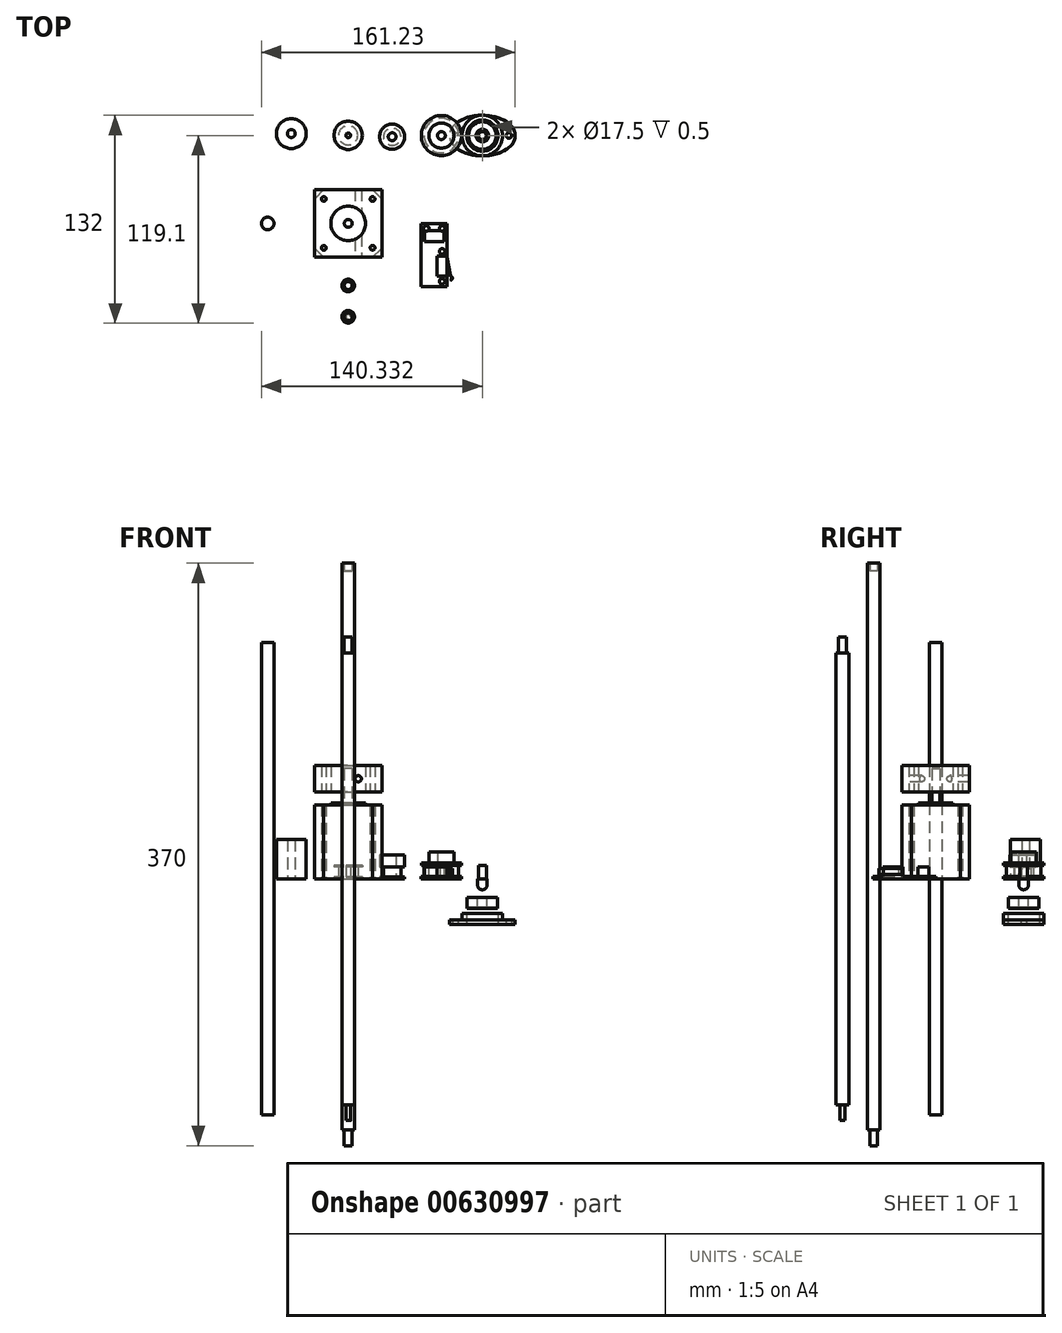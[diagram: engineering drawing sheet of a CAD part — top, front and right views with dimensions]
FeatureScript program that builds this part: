
annotation { "Feature Type Name" : "Feature", "Feature Type Description" : "" }
export const myFeature = defineFeature(function(context is Context, id is Id, definition is map)
    precondition{}
    {
        {
            var Q0;
            Q0=qCreatedBy(makeId("Top.planeOp"),FACE);
            var sketch = newSketch(context, id + "F0", { "sketchPlane" : qUnion([Q0])});
            skLineSegment(sketch, "E0.bottom", {"start": v(-21.5, 21.5) * mm, "end": v(21.5, 21.5) * mm});
            skLineSegment(sketch, "E0.top", {"start": v(-21.5, -21.5) * mm, "end": v(21.5, -21.5) * mm});
            skLineSegment(sketch, "E0.left", {"start": v(-21.5, 21.5) * mm, "end": v(-21.5, -21.5) * mm});
            skLineSegment(sketch, "E0.right", {"start": v(21.5, 21.5) * mm, "end": v(21.5, -21.5) * mm});
            skPoint(sketch, "E0.middle", {"position": v(0, 0) * mm});
            skLineSegment(sketch, "E1.bottom", {"start": v(15.5, 15.5) * mm, "end": v(-15.5, 15.5) * mm, "construction": true});
            skLineSegment(sketch, "E1.top", {"start": v(15.5, -15.5) * mm, "end": v(-15.5, -15.5) * mm, "construction": true});
            skLineSegment(sketch, "E1.left", {"start": v(15.5, 15.5) * mm, "end": v(15.5, -15.5) * mm, "construction": true});
            skLineSegment(sketch, "E1.right", {"start": v(-15.5, 15.5) * mm, "end": v(-15.5, -15.5) * mm, "construction": true});
            skCircle(sketch, "E2", {"center": v(-15.5, 15.5) * mm, "radius": 1.5 * mm});
            skCircle(sketch, "E3", {"center": v(15.5, 15.5) * mm, "radius": 1.5 * mm});
            skCircle(sketch, "E4", {"center": v(15.5, -15.5) * mm, "radius": 1.5 * mm});
            skCircle(sketch, "E5", {"center": v(-15.5, -15.5) * mm, "radius": 1.5 * mm});
            skSolve(sketch);
        }
        {
            var Q0;
            Q0=makeQuery(id+"F0.imprint","IMPRINT",FACE,{"disambiguationData":[TD([[makeQuery(id+"F0.imprint","IMPRINT",EDGE,{"derivedFrom":sQuery(id+"F0.wireOp",EDGE,"E0.bottom")}),-1.0]])]});
            extrude(context, id + "F1", {"entities" : qUnion([Q0]), "depth" : 47 * mm, "offsetDistance" : 25 * mm});
        }
        {
            var Q0;
            Q0=makeQuery(id+"F1.opExtrude","CAP_FACE",FACE,{"disambiguationData":[OSD([sQuery(id+"F0.wireOp",EDGE,"E0.bottom"),sQuery(id+"F0.wireOp",EDGE,"E0.top"),sQuery(id+"F0.wireOp",EDGE,"E0.left"),sQuery(id+"F0.wireOp",EDGE,"E0.right")])],"isStart":false});
            var sketch = newSketch(context, id + "F2", { "sketchPlane" : qUnion([Q0])});
            skCircle(sketch, "E6", {"center": v(0, 0) * mm, "radius": 11 * mm});
            skCircle(sketch, "E7", {"center": v(0, 0) * mm, "radius": 2.5 * mm});
            skSolve(sketch);
        }
        {
            var Q0;
            Q0=makeQuery(id+"F2.imprint","IMPRINT",FACE,{"disambiguationData":[TD([[makeQuery(id+"F2.imprint","IMPRINT",EDGE,{"derivedFrom":sQuery(id+"F2.wireOp",EDGE,"E7")}),1.0]])]});
            extrude(context, id + "F3", {"entities" : qUnion([Q0]), "operationType" : NewBodyOperationType.ADD, "depth" : 23 * mm, "offsetDistance" : 25 * mm});
        }
        {
            var Q0;
            Q0=makeQuery(id+"F2.imprint","IMPRINT",FACE,{"disambiguationData":[TD([[makeQuery(id+"F2.imprint","IMPRINT",EDGE,{"derivedFrom":sQuery(id+"F2.wireOp",EDGE,"E6")}),1.0]])]});
            extrude(context, id + "F4", {"entities" : qUnion([Q0]), "operationType" : NewBodyOperationType.ADD, "depth" : 1 * mm, "offsetDistance" : 25 * mm});
        }
        {
            var Q0;
            Q0=makeQuery(id+"F1.opExtrude","SWEPT_EDGE",EDGE,{"disambiguationData":[OSD([sQuery(id+"F0.wireOp",EDGE,"E0.top"),sQuery(id+"F0.wireOp",EDGE,"E0.right")])]});
            var Q1;
            Q1=makeQuery(id+"F1.opExtrude","SWEPT_EDGE",EDGE,{"disambiguationData":[OSD([sQuery(id+"F0.wireOp",EDGE,"E0.top"),sQuery(id+"F0.wireOp",EDGE,"E0.left")])]});
            var Q2;
            Q2=makeQuery(id+"F1.opExtrude","SWEPT_EDGE",EDGE,{"disambiguationData":[OSD([sQuery(id+"F0.wireOp",EDGE,"E0.bottom"),sQuery(id+"F0.wireOp",EDGE,"E0.left")])]});
            var Q3;
            Q3=makeQuery(id+"F1.opExtrude","SWEPT_EDGE",EDGE,{"disambiguationData":[OSD([sQuery(id+"F0.wireOp",EDGE,"E0.bottom"),sQuery(id+"F0.wireOp",EDGE,"E0.right")])]});
            chamfer(context, id + "F5", {"entities" : qUnion([Q0, Q1, Q2, Q3]), "width" : 6 * mm});
        }
        {
            var Q0;
            Q0=makeQuery(id+"F0.imprint","IMPRINT",FACE,{"disambiguationData":[TD([[makeQuery(id+"F0.imprint","IMPRINT",EDGE,{"derivedFrom":sQuery(id+"F0.wireOp",EDGE,"E2")}),1.0]])]});
            var Q1;
            Q1=makeQuery(id+"F0.imprint","IMPRINT",FACE,{"disambiguationData":[TD([[makeQuery(id+"F0.imprint","IMPRINT",EDGE,{"derivedFrom":sQuery(id+"F0.wireOp",EDGE,"E3")}),1.0]])]});
            var Q2;
            Q2=makeQuery(id+"F0.imprint","IMPRINT",FACE,{"disambiguationData":[TD([[makeQuery(id+"F0.imprint","IMPRINT",EDGE,{"derivedFrom":sQuery(id+"F0.wireOp",EDGE,"E4")}),1.0]])]});
            var Q3;
            Q3=makeQuery(id+"F0.imprint","IMPRINT",FACE,{"disambiguationData":[TD([[makeQuery(id+"F0.imprint","IMPRINT",EDGE,{"derivedFrom":sQuery(id+"F0.wireOp",EDGE,"E5")}),1.0]])]});
            extrude(context, id + "F6", {"entities" : qUnion([Q0, Q1, Q2, Q3]), "operationType" : NewBodyOperationType.REMOVE, "depth" : 50 * mm, "offsetDistance" : 25 * mm});
        }
        {
            var Q0;
            Q0=qCreatedBy(makeId("Top.planeOp"),FACE);
            var sketch = newSketch(context, id + "F7", { "sketchPlane" : qUnion([Q0])});
            skPoint(sketch, "E8", {"position": v(0, 55.95) * mm});
            skCircle(sketch, "E9", {"center": v(0, 55.95) * mm, "radius": 1.5 * mm});
            skCircle(sketch, "E10", {"center": v(0, 55.95) * mm, "radius": 6.1 * mm});
            skCircle(sketch, "E11", {"center": v(0, 55.95) * mm, "radius": 9 * mm});
            skPoint(sketch, "E12", {"position": v(59.2, 55.95) * mm});
            skSolve(sketch);
        }
        {
            var Q0;
            Q0=makeQuery(id+"F7.imprint","IMPRINT",FACE,{"disambiguationData":[TD([[makeQuery(id+"F7.imprint","IMPRINT",EDGE,{"derivedFrom":sQuery(id+"F7.wireOp",EDGE,"E10")}),-1.0]])]});
            extrude(context, id + "F8", {"entities" : qUnion([Q0]), "depth" : 1 * mm, "offsetDistance" : 25 * mm});
        }
        {
            var Q0;
            Q0=makeQuery(id+"F7.imprint","IMPRINT",FACE,{"disambiguationData":[TD([[makeQuery(id+"F7.imprint","IMPRINT",EDGE,{"derivedFrom":sQuery(id+"F7.wireOp",EDGE,"E9")}),-1.0]])]});
            extrude(context, id + "F9", {"entities" : qUnion([Q0]), "operationType" : NewBodyOperationType.ADD, "depth" : 8.5 * mm, "offsetDistance" : 25 * mm});
        }
        {
            var Q0;
            Q0=makeQuery(id+"F7.imprint","IMPRINT",FACE,{"disambiguationData":[TD([[makeQuery(id+"F7.imprint","IMPRINT",EDGE,{"derivedFrom":sQuery(id+"F7.wireOp",EDGE,"E10")}),-1.0]])]});
            extrude(context, id + "F10", {"entities" : qUnion([Q0]), "operationType" : NewBodyOperationType.ADD, "depth" : 8.5 * mm, "offsetDistance" : 25 * mm, "hasSecondDirection" : true, "secondDirectionOppositeDirection" : false, "secondDirectionDepth" : 7.5 * mm});
        }
        {
            var Q0;
            Q0=qCreatedBy(makeId("Top.planeOp"),FACE);
            var sketch = newSketch(context, id + "F11", { "sketchPlane" : qUnion([Q0])});
            skPoint(sketch, "E13", {"position": v(27.93, 55.05) * mm});
            skCircle(sketch, "E14", {"center": v(27.93, 55.05) * mm, "radius": 2.5 * mm});
            skCircle(sketch, "E15", {"center": v(27.93, 55.05) * mm, "radius": 5.5 * mm});
            skCircle(sketch, "E16", {"center": v(27.93, 55.05) * mm, "radius": 8 * mm});
            skSolve(sketch);
        }
        {
            var Q0;
            Q0=makeQuery(id+"F11.imprint","IMPRINT",FACE,{"disambiguationData":[TD([[makeQuery(id+"F11.imprint","IMPRINT",EDGE,{"derivedFrom":sQuery(id+"F11.wireOp",EDGE,"E15")}),-1.0]])]});
            extrude(context, id + "F12", {"entities" : qUnion([Q0]), "depth" : 1 * mm, "offsetDistance" : 25 * mm});
        }
        {
            var Q0;
            Q0=makeQuery(id+"F11.imprint","IMPRINT",FACE,{"disambiguationData":[TD([[makeQuery(id+"F11.imprint","IMPRINT",EDGE,{"derivedFrom":sQuery(id+"F11.wireOp",EDGE,"E14")}),-1.0]])]});
            extrude(context, id + "F13", {"entities" : qUnion([Q0]), "operationType" : NewBodyOperationType.ADD, "depth" : 15 * mm, "offsetDistance" : 25 * mm});
        }
        {
            var Q0;
            Q0=makeQuery(id+"F11.imprint","IMPRINT",FACE,{"disambiguationData":[TD([[makeQuery(id+"F11.imprint","IMPRINT",EDGE,{"derivedFrom":sQuery(id+"F11.wireOp",EDGE,"E15")}),-1.0]])]});
            extrude(context, id + "F14", {"entities" : qUnion([Q0]), "operationType" : NewBodyOperationType.ADD, "depth" : 15 * mm, "offsetDistance" : 25 * mm, "hasSecondDirection" : true, "secondDirectionOppositeDirection" : false, "secondDirectionDepth" : 7.5 * mm});
        }
        {
            var Q0;
            Q0=makeQuery(id+"F2.imprint","IMPRINT",FACE,{"disambiguationData":[TD([[makeQuery(id+"F2.imprint","IMPRINT",EDGE,{"derivedFrom":sQuery(id+"F2.wireOp",EDGE,"E6")}),-1.0]])]});
            extrude(context, id + "F15", {"entities" : qUnion([Q0]), "depth" : 25 * mm, "offsetDistance" : 25 * mm, "hasSecondDirection" : true, "secondDirectionOppositeDirection" : false, "secondDirectionDepth" : 8 * mm});
        }
        {
            var Q0;
            Q0=makeQuery(id+"F15.opExtrude","SWEPT_FACE",FACE,{"disambiguationData":[OSD([sQuery(id+"F0.wireOp",EDGE,"E0.top")])]});
            var sketch = newSketch(context, id + "F16", { "sketchPlane" : qUnion([Q0])});
            skCircle(sketch, "E17", {"center": v(6.4, 63.5) * mm, "radius": 2 * mm});
            skPoint(sketch, "E17.centerSnap0", {"position": v(21.5, 63.5) * mm});
            skSolve(sketch);
        }
        {
            var Q0;
            Q0=makeQuery(id+"F16.imprint","IMPRINT",FACE,{"disambiguationData":[TD([[makeQuery(id+"F16.imprint","IMPRINT",EDGE,{"derivedFrom":sQuery(id+"F16.wireOp",EDGE,"E17")}),1.0]])]});
            extrude(context, id + "F17", {"entities" : qUnion([Q0]), "operationType" : NewBodyOperationType.REMOVE, "oppositeDirection" : true, "depth" : 50 * mm, "offsetDistance" : 25 * mm});
        }
        {
            var Q0;
            Q0=qCreatedBy(makeId("Top.planeOp"),FACE);
            var sketch = newSketch(context, id + "F18", { "sketchPlane" : qUnion([Q0])});
            skCircle(sketch, "E18", {"center": v(-36.13, 57.04) * mm, "radius": 9.5 * mm});
            skCircle(sketch, "E19", {"center": v(-36.13, 57.04) * mm, "radius": 2.5 * mm});
            skSolve(sketch);
        }
        {
            var Q0;
            Q0=makeQuery(id+"F18.imprint","IMPRINT",FACE,{"disambiguationData":[TD([[makeQuery(id+"F18.imprint","IMPRINT",EDGE,{"derivedFrom":sQuery(id+"F18.wireOp",EDGE,"E18")}),1.0]])]});
            extrude(context, id + "F19", {"entities" : qUnion([Q0]), "depth" : 25 * mm, "offsetDistance" : 25 * mm});
        }
        {
            var Q0;
            Q0=qCreatedBy(makeId("Top.planeOp"),FACE);
            var sketch = newSketch(context, id + "F20", { "sketchPlane" : qUnion([Q0])});
            skCircle(sketch, "E20", {"center": v(-51.13, 0) * mm, "radius": 4 * mm});
            skSolve(sketch);
        }
        {
            var Q0;
            Q0=makeQuery(id+"F20.imprint","IMPRINT",FACE,{"disambiguationData":[TD([[makeQuery(id+"F20.imprint","IMPRINT",EDGE,{"derivedFrom":sQuery(id+"F20.wireOp",EDGE,"E20")}),1.0]])]});
            extrude(context, id + "F21", {"entities" : qUnion([Q0]), "depth" : 300 * mm, "offsetDistance" : 25 * mm, "symmetric" : true});
        }
        {
            var Q0;
            Q0=qCreatedBy(makeId("Top.planeOp"),FACE);
            var sketch = newSketch(context, id + "F22", { "sketchPlane" : qUnion([Q0])});
            skLineSegment(sketch, "E21.bottom", {"start": v(46.4, -40) * mm, "end": v(62.9, -40) * mm});
            skLineSegment(sketch, "E21.top", {"start": v(46.4, 0) * mm, "end": v(62.9, 0) * mm});
            skLineSegment(sketch, "E21.left", {"start": v(46.4, -40) * mm, "end": v(46.4, 0) * mm});
            skLineSegment(sketch, "E21.right", {"start": v(62.9, -40) * mm, "end": v(62.9, 0) * mm});
            skCircle(sketch, "E22", {"center": v(49.66, -3.25) * mm, "radius": 1.75 * mm});
            skCircle(sketch, "E23", {"center": v(59.66, -3.25) * mm, "radius": 1.75 * mm});
            skCircle(sketch, "E24", {"center": v(59.66, -17.75) * mm, "radius": 1.75 * mm});
            skCircle(sketch, "E25", {"center": v(59.66, -36.75) * mm, "radius": 1.75 * mm});
            skLineSegment(sketch, "E26.bottom", {"start": v(48.4, -11.5) * mm, "end": v(60.9, -11.5) * mm});
            skLineSegment(sketch, "E26.top", {"start": v(48.4, -4.5) * mm, "end": v(60.9, -4.5) * mm});
            skLineSegment(sketch, "E26.left", {"start": v(48.4, -11.5) * mm, "end": v(48.4, -4.5) * mm});
            skLineSegment(sketch, "E26.right", {"start": v(60.9, -11.5) * mm, "end": v(60.9, -4.5) * mm});
            skPoint(sketch, "E26.middle", {"position": v(54.66, -8) * mm});
            skPoint(sketch, "E26.middle.positionSnap0", {"position": v(54.66, 0) * mm});
            skPoint(sketch, "E26.centerSnap0", {"position": v(54.66, 0) * mm});
            skLineSegment(sketch, "E27.bottom", {"start": v(62.9, -33.6) * mm, "end": v(56.4, -33.6) * mm});
            skLineSegment(sketch, "E27.top", {"start": v(62.9, -20.8) * mm, "end": v(56.4, -20.8) * mm});
            skLineSegment(sketch, "E27.left", {"start": v(62.9, -33.6) * mm, "end": v(62.9, -20.8) * mm});
            skLineSegment(sketch, "E27.right", {"start": v(56.4, -33.6) * mm, "end": v(56.4, -20.8) * mm});
            skPoint(sketch, "E27.middle", {"position": v(59.66, -27.2) * mm});
            skSolve(sketch);
        }
        {
            var Q0;
            Q0=makeQuery(id+"F22.imprint","IMPRINT",FACE,{"disambiguationData":[TD([[makeQuery(id+"F22.imprint","IMPRINT",EDGE,{"derivedFrom":sQuery(id+"F22.wireOp",EDGE,"E26.bottom")}),1.0]])]});
            var Q1;
            Q1=makeQuery(id+"F22.imprint","IMPRINT",FACE,{"disambiguationData":[TD([[makeQuery(id+"F22.imprint","IMPRINT",EDGE,{"derivedFrom":sQuery(id+"F22.wireOp",EDGE,"E27.bottom")}),-1.0]])]});
            extrude(context, id + "F23", {"entities" : qUnion([Q0, Q1]), "depth" : 7.5 * mm, "offsetDistance" : 25 * mm});
        }
        {
            var Q0;
            {var subQ11=sQuery(id+"F22.wireOp",EDGE,"E21.bottom");Q0=makeQuery(id+"F22.imprint","IMPRINT",FACE,{"disambiguationData":[TD([[makeQuery(id+"F22.imprint","IMPRINT",EDGE,{"derivedFrom":subQ11}),1.0]])]});}
            extrude(context, id + "F24", {"entities" : qUnion([Q0]), "operationType" : NewBodyOperationType.ADD, "depth" : 1.6 * mm, "offsetDistance" : 25 * mm});
        }
        {
            var Q0;
            Q0=makeQuery(id+"F24.opExtrude","CAP_FACE",FACE,{"disambiguationData":[OSD([sQuery(id+"F22.wireOp",EDGE,"E21.bottom"),sQuery(id+"F22.wireOp",EDGE,"E21.top"),sQuery(id+"F22.wireOp",EDGE,"E21.left"),sQuery(id+"F22.wireOp",EDGE,"E21.right"),sQuery(id+"F22.wireOp",EDGE,"E22"),sQuery(id+"F22.wireOp",EDGE,"E23"),sQuery(id+"F22.wireOp",EDGE,"E24"),sQuery(id+"F22.wireOp",EDGE,"E25"),sQuery(id+"F22.wireOp",EDGE,"E26.bottom"),sQuery(id+"F22.wireOp",EDGE,"E26.top"),sQuery(id+"F22.wireOp",EDGE,"E26.left"),sQuery(id+"F22.wireOp",EDGE,"E26.right"),sQuery(id+"F22.wireOp",EDGE,"E27.bottom"),sQuery(id+"F22.wireOp",EDGE,"E27.top"),sQuery(id+"F22.wireOp",EDGE,"E27.right")])],"isStart":false});
            var sketch = newSketch(context, id + "F25", { "sketchPlane" : qUnion([Q0])});
            skLineSegment(sketch, "E28", {"start": v(62.9, -21.35) * mm, "end": v(65, -33.28) * mm});
            skLineSegment(sketch, "E29", {"start": v(64.69, -33.6) * mm, "end": v(62.56, -21.47) * mm});
            skLineSegment(sketch, "E30", {"start": v(62.56, -21.47) * mm, "end": v(62.9, -21.35) * mm});
            skLineSegment(sketch, "E31", {"start": v(65.24, -36.03) * mm, "end": v(65, -35.72) * mm});
            skArc(sketch, "E32", {"start": v(65, -35.72) * mm, "mid": v(65.72, -34.53) * mm, "end": v(64.69, -33.6) * mm});
            skArc(sketch, "E33", {"start": v(65.24, -36.03) * mm, "mid": v(66.14, -34.57) * mm, "end": v(65, -33.28) * mm});
            skSolve(sketch);
        }
        {
            var Q0;
            Q0=makeQuery(id+"F25.imprint","IMPRINT",FACE,{"disambiguationData":[TD([[makeQuery(id+"F25.imprint","IMPRINT",EDGE,{"derivedFrom":sQuery(id+"F25.wireOp",EDGE,"E28")}),-1.0]])]});
            extrude(context, id + "F26", {"entities" : qUnion([Q0]), "operationType" : NewBodyOperationType.ADD, "depth" : 5 * mm, "offsetDistance" : 25 * mm, "hasSecondDirection" : true, "secondDirectionOppositeDirection" : false, "secondDirectionDepth" : 1 * mm});
        }
        {
            var Q0;
            Q0=qCreatedBy(makeId("Front.planeOp"),FACE);
            cPlane(context, id + "F27", {"entities" : qUnion([Q0]), "cplaneType" : CPlaneType.OFFSET, "offset" : 55.8 * mm, "oppositeDirection" : true, "width" : 150 * mm, "height" : 150 * mm});
        }
        {
            var Q0;
            Q0=qCreatedBy(id+"F27.planeOp",FACE);
            var sketch = newSketch(context, id + "F28", { "sketchPlane" : qUnion([Q0])});
            skPoint(sketch, "E34", {"position": v(59.2, 0) * mm});
            skLineSegment(sketch, "E35", {"start": v(59.2, 0) * mm, "end": v(59.2, 17) * mm});
            skLineSegment(sketch, "E36", {"start": v(59.2, 17) * mm, "end": v(67.2, 17) * mm});
            skLineSegment(sketch, "E37", {"start": v(67.2, 17) * mm, "end": v(67.2, 10) * mm});
            skLineSegment(sketch, "E38", {"start": v(67.2, 10) * mm, "end": v(71.95, 10) * mm});
            skLineSegment(sketch, "E39", {"start": v(71.95, 10) * mm, "end": v(71.95, 8.5) * mm});
            skLineSegment(sketch, "E40", {"start": v(71.95, 8.5) * mm, "end": v(70.2, 8.5) * mm});
            skLineSegment(sketch, "E41", {"start": v(70.2, 8.5) * mm, "end": v(70.2, 1.5) * mm});
            skLineSegment(sketch, "E42", {"start": v(70.2, 1.5) * mm, "end": v(71.95, 1.5) * mm});
            skLineSegment(sketch, "E43", {"start": v(71.95, 1.5) * mm, "end": v(71.95, 0) * mm});
            skLineSegment(sketch, "E44", {"start": v(71.95, 0) * mm, "end": v(59.2, 0) * mm});
            skLineSegment(sketch, "E45", {"start": v(61.7, 17) * mm, "end": v(61.7, 0) * mm});
            skLineSegment(sketch, "E46", {"start": v(88.2, 0) * mm, "end": v(87.7, 0) * mm});
            skLineSegment(sketch, "E47", {"start": v(87.7, 0) * mm, "end": v(87.7, 8.5) * mm});
            skLineSegment(sketch, "E48", {"start": v(87.7, 8.5) * mm, "end": v(85.2, 8.5) * mm});
            skLineSegment(sketch, "E49", {"start": v(85.2, 8.5) * mm, "end": v(85.2, -7) * mm});
            skLineSegment(sketch, "E50", {"start": v(88.2, -4) * mm, "end": v(88.2, 0) * mm});
            skArc(sketch, "E51", {"start": v(88.2, -4) * mm, "mid": v(87.32, -6.12) * mm, "end": v(85.2, -7) * mm});
            skLineSegment(sketch, "E52", {"start": v(88.2, -11.77) * mm, "end": v(89.2, -11.77) * mm});
            skLineSegment(sketch, "E53", {"start": v(89.2, -11.77) * mm, "end": v(89.2, -12.27) * mm});
            skLineSegment(sketch, "E54", {"start": v(89.2, -12.27) * mm, "end": v(93.95, -12.27) * mm});
            skLineSegment(sketch, "E55", {"start": v(93.95, -12.27) * mm, "end": v(93.95, -11.77) * mm});
            skLineSegment(sketch, "E56", {"start": v(93.95, -11.77) * mm, "end": v(94.95, -11.77) * mm});
            skLineSegment(sketch, "E57", {"start": v(94.95, -11.77) * mm, "end": v(94.95, -18.77) * mm});
            skLineSegment(sketch, "E58", {"start": v(94.95, -18.77) * mm, "end": v(93.95, -18.77) * mm});
            skLineSegment(sketch, "E59", {"start": v(93.95, -18.77) * mm, "end": v(93.95, -18.27) * mm});
            skLineSegment(sketch, "E60", {"start": v(93.95, -18.27) * mm, "end": v(89.2, -18.27) * mm});
            skLineSegment(sketch, "E61", {"start": v(89.2, -18.27) * mm, "end": v(89.2, -18.77) * mm});
            skLineSegment(sketch, "E62", {"start": v(89.2, -18.77) * mm, "end": v(88.2, -18.77) * mm});
            skLineSegment(sketch, "E63", {"start": v(88.2, -18.77) * mm, "end": v(88.2, -11.77) * mm});
            skLineSegment(sketch, "E64", {"start": v(85.2, -11.77) * mm, "end": v(85.2, -18.77) * mm});
            skSolve(sketch);
        }
        {
            var Q0;
            {var subQ0=sQuery(id+"F28.wireOp",EDGE,"E37");Q0=makeQuery(id+"F28.imprint","IMPRINT",FACE,{"disambiguationData":[TD([[makeQuery(id+"F28.imprint","IMPRINT",EDGE,{"derivedFrom":subQ0}),-1.0]])]});}
            var Q1;
            Q1=sQuery(id+"F28.wireOp",EDGE,"E35");
            revolve(context, id + "F29", {"surfaceOperationType" : NewSurfaceOperationType.NEW, "entities" : qUnion([Q0]), "axis" : qUnion([Q1]), "revolveType" : RevolveType.FULL});
        }
        {
            var Q0;
            Q0=makeQuery(id+"F28.imprint","IMPRINT",FACE,{"disambiguationData":[TD([[makeQuery(id+"F28.imprint","IMPRINT",EDGE,{"derivedFrom":sQuery(id+"F28.wireOp",EDGE,"E46")}),1.0]])]});
            var Q1;
            Q1=sQuery(id+"F28.wireOp",EDGE,"E49");
            revolve(context, id + "F30", {"surfaceOperationType" : NewSurfaceOperationType.NEW, "entities" : qUnion([Q0]), "axis" : qUnion([Q1]), "revolveType" : RevolveType.FULL});
        }
        {
            var Q0;
            Q0=makeQuery(id+"F28.imprint","IMPRINT",FACE,{"disambiguationData":[TD([[makeQuery(id+"F28.imprint","IMPRINT",EDGE,{"derivedFrom":sQuery(id+"F28.wireOp",EDGE,"E52")}),-1.0]])]});
            var Q1;
            Q1=sQuery(id+"F28.wireOp",EDGE,"E64");
            revolve(context, id + "F31", {"surfaceOperationType" : NewSurfaceOperationType.NEW, "entities" : qUnion([Q0]), "axis" : qUnion([Q1]), "revolveType" : RevolveType.FULL});
        }
        {
            var Q0;
            Q0=qCreatedBy(makeId("Top.planeOp"),FACE);
            cPlane(context, id + "F32", {"entities" : qUnion([Q0]), "cplaneType" : CPlaneType.OFFSET, "offset" : 29 * mm, "oppositeDirection" : true, "width" : 150 * mm, "height" : 150 * mm});
        }
        {
            var Q0;
            Q0=qCreatedBy(id+"F32.planeOp",FACE);
            var sketch = newSketch(context, id + "F33", { "sketchPlane" : qUnion([Q0])});
            skPoint(sketch, "E65", {"position": v(85.2, 55.8) * mm});
            skCircle(sketch, "E66", {"center": v(85.2, 55.8) * mm, "radius": 9.9 * mm});
            skPoint(sketch, "E67", {"position": v(94.95, 55.81) * mm});
            skCircle(sketch, "E68", {"center": v(85.2, 55.8) * mm, "radius": 12.9 * mm});
            skEllipse(sketch, "E69", {"center": v(85.2, 55.8) * mm, "majorRadius": 20.9 * mm, "minorRadius": 12.9 * mm, "majorAxis": v(1, 0)});
            skPoint(sketch, "E70", {"position": v(102.1, 55.8) * mm});
            skPoint(sketch, "E71", {"position": v(68.1, 55.8) * mm});
            skPoint(sketch, "E72", {"position": v(106.1, 55.8) * mm});
            skCircle(sketch, "E73", {"center": v(68.1, 55.8) * mm, "radius": 1.75 * mm});
            skCircle(sketch, "E74", {"center": v(102.1, 55.8) * mm, "radius": 1.75 * mm});
            skSolve(sketch);
        }
        {
            var Q0;
            Q0=makeQuery(id+"F33.imprint","IMPRINT",FACE,{"disambiguationData":[TD([[makeQuery(id+"F33.imprint","IMPRINT",EDGE,{"derivedFrom":sQuery(id+"F33.wireOp",EDGE,"E66")}),-1.0]])]});
            extrude(context, id + "F34", {"entities" : qUnion([Q0]), "depth" : 7 * mm, "offsetDistance" : 25 * mm});
        }
        {
            var Q0;
            Q0=makeQuery(id+"F33.imprint","IMPRINT",FACE,{"disambiguationData":[TD([[makeQuery(id+"F33.imprint","IMPRINT",EDGE,{"derivedFrom":sQuery(id+"F33.wireOp",EDGE,"E74")}),-1.0]])]});
            var Q1;
            Q1=makeQuery(id+"F33.imprint","IMPRINT",FACE,{"disambiguationData":[TD([[makeQuery(id+"F33.imprint","IMPRINT",EDGE,{"derivedFrom":sQuery(id+"F33.wireOp",EDGE,"E73")}),-1.0]])]});
            extrude(context, id + "F35", {"entities" : qUnion([Q0, Q1]), "operationType" : NewBodyOperationType.ADD, "depth" : 3 * mm, "offsetDistance" : 25 * mm});
        }
        {
            var Q0;
            Q0=qCreatedBy(makeId("Right.planeOp"),FACE);
            var sketch = newSketch(context, id + "F36", { "sketchPlane" : qUnion([Q0])});
            skLineSegment(sketch, "E75", {"start": v(-59.3, 153.5) * mm, "end": v(-59.3, -153.5) * mm});
            skLineSegment(sketch, "E76", {"start": v(-59.3, -153.5) * mm, "end": v(-57.8, -153.5) * mm});
            skLineSegment(sketch, "E77", {"start": v(-57.8, -153.5) * mm, "end": v(-57.8, -143.5) * mm});
            skLineSegment(sketch, "E78", {"start": v(-57.8, -143.5) * mm, "end": v(-55.3, -143.5) * mm});
            skLineSegment(sketch, "E79", {"start": v(-55.3, 143.5) * mm, "end": v(-56.8, 143.5) * mm});
            skLineSegment(sketch, "E80", {"start": v(-56.8, 143.5) * mm, "end": v(-56.8, 153.5) * mm});
            skLineSegment(sketch, "E81", {"start": v(-56.8, 153.5) * mm, "end": v(-59.3, 153.5) * mm});
            skLineSegment(sketch, "E82", {"start": v(-55.3, -143.5) * mm, "end": v(-55.3, 0) * mm});
            skLineSegment(sketch, "E83", {"start": v(-55.3, 0) * mm, "end": v(-55.3, 143.5) * mm});
            skLineSegment(sketch, "E84", {"start": v(-39.45, -169.54) * mm, "end": v(-39.45, 195.46) * mm});
            skLineSegment(sketch, "E85", {"start": v(-39.45, 195.46) * mm, "end": v(-36.95, 195.46) * mm});
            skLineSegment(sketch, "E86", {"start": v(-36.95, 195.46) * mm, "end": v(-36.95, 200.46) * mm});
            skLineSegment(sketch, "E87", {"start": v(-36.95, 200.46) * mm, "end": v(-35.45, 200.46) * mm});
            skLineSegment(sketch, "E88", {"start": v(-35.45, 200.46) * mm, "end": v(-35.45, -159.54) * mm});
            skLineSegment(sketch, "E89", {"start": v(-35.45, -159.54) * mm, "end": v(-36.95, -159.54) * mm});
            skLineSegment(sketch, "E90", {"start": v(-36.95, -159.54) * mm, "end": v(-36.95, -169.54) * mm});
            skLineSegment(sketch, "E91", {"start": v(-36.95, -169.54) * mm, "end": v(-39.45, -169.54) * mm});
            skSolve(sketch);
        }
        {
            var Q0;
            Q0=makeQuery(id+"F36.imprint","IMPRINT",FACE,{"disambiguationData":[TD([[makeQuery(id+"F36.imprint","IMPRINT",EDGE,{"derivedFrom":sQuery(id+"F36.wireOp",EDGE,"E75")}),1.0]])]});
            var Q1;
            Q1=sQuery(id+"F36.wireOp",EDGE,"E75");
            revolve(context, id + "F37", {"surfaceOperationType" : NewSurfaceOperationType.NEW, "entities" : qUnion([Q0]), "axis" : qUnion([Q1]), "revolveType" : RevolveType.FULL});
        }
        {
            var Q0;
            Q0=makeQuery(id+"F36.imprint","IMPRINT",FACE,{"disambiguationData":[TD([[makeQuery(id+"F36.imprint","IMPRINT",EDGE,{"derivedFrom":sQuery(id+"F36.wireOp",EDGE,"E84")}),-1.0]])]});
            var Q1;
            Q1=sQuery(id+"F36.wireOp",EDGE,"E84");
            revolve(context, id + "F38", {"surfaceOperationType" : NewSurfaceOperationType.NEW, "entities" : qUnion([Q0]), "axis" : qUnion([Q1]), "revolveType" : RevolveType.FULL});
        }
    });
